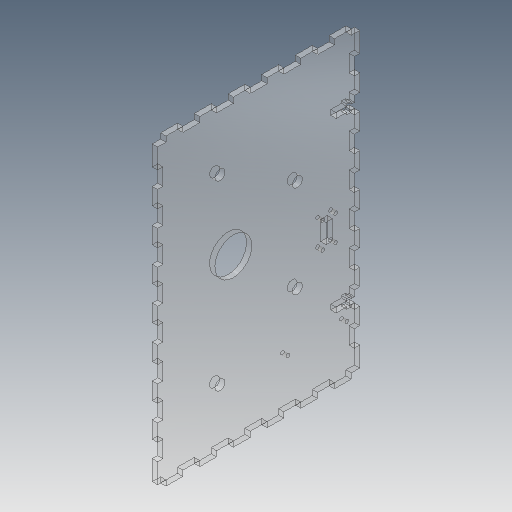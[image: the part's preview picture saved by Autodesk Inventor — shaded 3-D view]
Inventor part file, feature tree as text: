
AUTODESK INVENTOR PART (.ipt)
format: ipt  version: 2018 (Build 220112000, 112)  size: 621,568 bytes
history: native  units: mm
features: sketch x9, projected_geometry x7, extrude x6, hole x4, mirror x3, pattern_linear x2
ambient origin geometry x8: Origin, YZ Plane, XZ Plane, XY Plane, X Axis, Y Axis, Z Axis, Center Point
bodies: Solid1 (feature_tree)
feature tree (31):
  extrude  "Extrusion1"  Depth=173.65mm
  extrude  "Extrusion4"  TaperAngle=0.0deg  [1 undecoded]
  pattern_linear  "Rectangular Pattern3"  Spacing1=60.0deg  [1 undecoded]
  mirror  "Mirror3"
  extrude  "Extrusion5"  TaperAngle=60.0deg  [1 undecoded]
  pattern_linear  "Rectangular Pattern4"  Spacing1=6.0mm  [1 undecoded]
  extrude  "Extrusion8"  Depth=10.0mm
  mirror  "Mirror4"
  hole  "Hole1"  [1 undecoded]
  sketch  "Sketch6"  dims[d4=95.0mm]
  hole  "Hole6"  [1 undecoded]
  extrude  "Extrusion6"  Depth=10.0mm TaperAngle=0.0deg
  mirror  "Mirror5"
  hole  "Hole9"  [1 undecoded]
  extrude  "Extrusion7"  Depth=20.0mm
  hole  "Hole10"  [1 undecoded]
  sketch  "Sketch1"  dims[d0=113.65mm d1=173.65mm]
  sketch  "Sketch2"  dims[d2=3.175mm d3=0.0mm]
  projected_geometry  "Projected Loop1"
  projected_geometry  "Projected Loop2"
  projected_geometry  "Projected Loop5"
  sketch  "Sketch10"  dims[d5=22.0mm]
  projected_geometry  "Projected Loop6"
  sketch  "Sketch11"  dims[d6=6.0mm d7=4.0mm d8=2.0mm d9=90.0deg d10=8.0mm d11=20.594885mm]
  projected_geometry  "Projected Loop7"
  sketch  "Sketch14"  dims[d12=41.825mm]
  sketch  "Sketch15"  dims[d40=3.0mm]
  projected_geometry  "Projected Loop8"
  sketch  "Sketch16"  dims[d41=5.5mm]
  projected_geometry  "Projected Loop9"
  sketch  "Sketch17"  dims[d42=2.5mm d74=60.0deg d75=60.0deg d77=6.0mm d78=6.0mm d79=4.0mm d80=2.0mm d81=90.0deg d82=8.0mm d83=20.594885mm d84=10.0mm d85=1.825mm d86=3.175mm d87=10.0mm d88=0.0mm d89=60.0mm d91=20.0mm d92=3.175mm d94=10.0mm d95=10.0mm d96=0.0mm d97=90.0mm d99=20.0mm d100=5.0mm d101=10.825mm d103=2.0mm d104=2.0mm d105=50.0mm d106=10.0mm d107=0.0mm d127=45.72mm d128=15.24mm d129=2.156mm d130=5.69mm d131=4.0mm d132=2.0mm d133=90.0deg d134=8.865mm d135=20.594885mm d136=1.905mm d137=1.905mm d138=11.43mm d139=3.81mm d140=10.0mm d141=0.0mm d142=7.62mm d143=10.0mm d144=0.0mm d145=2.156mm d146=5.69mm d147=4.0mm d148=2.0mm d149=90.0deg d150=8.865mm d151=20.594885mm]
note: 8 required parameter values undecoded (feature->parameter linkage not recoverable at this tier; creation-order binding heuristic only, values carry confidence <= 0.55)
